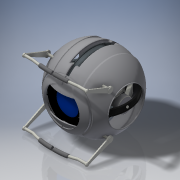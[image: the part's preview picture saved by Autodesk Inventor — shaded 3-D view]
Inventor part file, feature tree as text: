
AUTODESK INVENTOR PART (.ipt)
format: ipt  version: 2019 (Build 230136000, 136)  size: 2,255,872 bytes
history: native  units: in
note: dims shown in document units (in); Inventor stores cm internally (conversion verified against a paired STEP export)
features: sketch x33, extrude x21, plane x10, other x9, chamfer x8, mirror x7, pattern_circular x4, fillet x3, revolve x2, sweep x2, projected_geometry x1
ambient origin geometry x8: Origin, YZ Plane, XZ Plane, XY Plane, X Axis, Y Axis, Z Axis, Center Point
bodies: Solid1 (feature_tree)
feature tree (100):
  other  "Wheatly 2.ipt"
  extrude  "Extrusion1"  Depth=2.75in
  extrude  "Extrusion3"  Depth=0.25in TaperAngle=0.0deg
  mirror  "Mirror1"
  extrude  "Extrusion4"  Depth=0.15in TaperAngle=0.0deg
  plane  "Work Plane1"
  extrude  "Extrusion5"  Depth=0.75in TaperAngle=0.0deg
  extrude  "Extrusion6"  Depth=2.5in
  sketch  "Sketch8"  dims[d18=0.25in d19=0.0in d20=2.3in]
  extrude  "Extrusion7"  Depth=2.3in
  extrude  "Extrusion8"  Depth=0.5375in TaperAngle=0.0deg
  extrude  "Extrusion9"  Depth=0.05in TaperAngle=0.0deg
  plane  "Work Plane2"
  extrude  "Extrusion10"  Depth=3.3in
  chamfer  "Chamfer1"  Distance=0.1in
  chamfer  "Chamfer2"  Distance=0.25in
  sketch  "Sketch13"  dims[d32=2.6in]
  pattern_circular  "Circular Pattern1"  Count=3 Angle=360.0deg
  pattern_circular  "Circular Pattern4"  Count=6 Angle=360.0deg
  chamfer  "Chamfer4"  Distance=0.25in
  chamfer  "Chamfer5"  Distance=0.25in
  chamfer  "Chamfer6"  Distance=0.25in
  chamfer  "Chamfer7"  Distance=0.25in
  plane  "Work Plane3"
  mirror  "Mirror2"
  pattern_circular  "Circular Pattern5"  Count=6 Angle=360.0deg
  extrude  "Extrusion11"  Depth=0.5in TaperAngle=0.0deg
  plane  "Work Plane4"
  revolve  "Revolution1"  Angle=90.0deg
  other  "Work Point4"
  plane  "Work Plane6"
  other  "Work Point5"
  other  "Work Point6"
  sketch  "Sketch16"  dims[d37=135.0deg]
  sketch  "Sketch17"  dims[d38=0.5in d39=0.25in d40=0.0in d41=0.0in]
  plane  "Work Plane7"
  mirror  "Mirror3"
  pattern_circular  "Circular Pattern6"  Count=3 Angle=360.0deg
  extrude  "Extrusion12"  Depth=0.25in
  sketch  "Sketch19"  dims[d45=0.25in d46=0.125in d47=0.1374in d48=1.1811in d49=360.0deg d60=2.3622in d61=360.0deg d63=0.25in d64=0.125in d65=0.1374in d66=0.25in d67=0.125in d68=0.1374in d69=0.25in d70=0.125in d71=0.1374in d72=0.25in d73=0.125in d74=0.1374in d75=2.3622in d76=360.0deg]
  extrude  "Extrusion13"  TaperAngle=90.0deg  [1 undecoded]
  mirror  "Mirror4"
  plane  "Work Plane8"
  plane  "Work Plane9"
  extrude  "Extrusion14"  Depth=0.2in
  extrude  "Extrusion15"  Depth=0.1in
  fillet  "Fillet1"  Radius=0.05in
  mirror  "Mirror5"
  extrude  "Extrusion16"  Depth=0.6in TaperAngle=0.0deg
  extrude  "Extrusion17"  Depth=1.1in
  extrude  "Extrusion18"  Depth=0.8in
  extrude  "Extrusion19"  Depth=0.05in TaperAngle=0.0deg
  chamfer  "Chamfer8"  Distance=0.05in
  chamfer  "Chamfer9"  Distance=0.04in
  plane  "Work Plane10"
  revolve  "Revolution2"  [1 undecoded]
  extrude  "Extrusion20"  Depth=1.9in
  extrude  "Extrusion21"  TaperAngle=90.0deg  [1 undecoded]
  extrude  "Extrusion22"  Depth=0.08in
  sketch  "Sketch31"  dims[d112=0.6in d113=0.05in d114=0.0in d115=0.05in d116=0.0in d117=0.04in d118=0.125in d119=0.1374in]
  plane  "Work Plane11"
  sweep  "Sweep1"
  sweep  "Sweep2"
  fillet  "Fillet2"  Radius=2.0in
  fillet  "Fillet3"  Radius=0.2in
  mirror  "Mirror6"
  mirror  "Mirror7"
  other  "Solid1::Wheatly 2.ipt"
  other  "TaggingFeature1"
  sketch  "Sketch2"  dims[d0=0.3937in d1=2.75in]
  sketch  "Sketch4"  dims[d2=3.3in d3=0.25in d4=0.0in]
  sketch  "Sketch5"  dims[d10=1.25in d11=0.15in d12=0.0in]
  sketch  "Sketch6"  dims[d13=3.3in d14=0.75in d15=0.0in]
  sketch  "Sketch7"  dims[d16=2.875in d17=2.5in]
  sketch  "Sketch9"  dims[d21=2.175in d22=0.5375in d23=0.0in]
  sketch  "Sketch10"  dims[d24=1.9in d25=0.05in d26=0.0in]
  sketch  "Sketch11"  dims[d27=2.3in d28=3.3in d29=0.1in d30=0.0in]
  projected_geometry  "Projected Loop3"
  sketch  "Sketch12"  dims[d31=3.2in]
  sketch  "Sketch14"  dims[d33=105.0deg d34=0.25in d35=0.0in]
  other  "Work Point1"
  other  "Work Point2"
  sketch  "Sketch15"  dims[d36=135.0deg]
  sketch  "Sketch18"  dims[d42=0.25in d43=0.125in d44=0.1374in]
  sketch  "Sketch20"  dims[d78=2.3622in d80=360.0deg d82=0.5in d83=0.0in]
  sketch  "Sketch21"  dims[d84=0.125in d85=90.0deg]
  sketch  "Sketch22"  dims[d86=90.0deg]
  sketch  "Sketch23"  dims[d87=0.03in d88=1.1811in d89=360.0deg]
  sketch  "Sketch24"  dims[d91=0.5in d92=0.0in d93=0.25in]
  sketch  "Sketch25"  dims[d94=90.0deg d95=90.0deg]
  sketch  "Sketch26"  dims[d96=0.75in d97=0.0in d98=0.2in]
  sketch  "Sketch27"  dims[d99=0.45in d100=0.0in d101=0.1in d102=0.05in d103=0.0in]
  sketch  "Sketch28"  dims[d104=1.0in d105=0.6in d106=0.0in]
  sketch  "Sketch29"  dims[d107=0.5in d108=1.1in]
  sketch  "Sketch30"  dims[d109=0.2in d110=0.0in d111=0.8in]
  other  "Work Point7"
  sketch  "Sketch32"  dims[d120=0.04in d121=0.125in d122=0.1374in d123=1.3in]
  sketch  "Sketch33"  dims[d124=0.1in d125=1.9in]
  sketch  "Sketch34"  dims[d126=0.1in d127=90.0deg]
  sketch  "Sketch35"  dims[d128=0.08in d129=0.08in d130=90.0deg d131=0.5in d132=2.0in d133=0.2in d136=0.9697in d137=0.3in d138=0.1in d139=0.0in d140=0.025in d141=0.125in d142=0.0in d143=0.0in d144=0.65in d145=0.0in d146=0.125in d147=0.125in d148=0.0in d149=0.0in d150=0.3in d151=0.0in d152=0.0in d153=0.1in d154=0.01in]
note: 3 required parameter values undecoded (feature->parameter linkage not recoverable at this tier; creation-order binding heuristic only, values carry confidence <= 0.55)